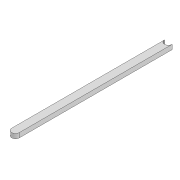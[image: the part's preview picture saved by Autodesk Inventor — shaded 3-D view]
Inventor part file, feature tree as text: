
AUTODESK INVENTOR PART (.ipt)
format: ipt  version: 2022 (Build 260153000, 153)  size: 77,824 bytes
history: native  units: mm
features: extrude x1, sketch x1
ambient origin geometry x8: Origin, YZ Plane, XZ Plane, XY Plane, X Axis, Y Axis, Z Axis, Center Point
bodies: Solid1 (feature_tree)
feature tree (2):
  extrude  "Extrusion1"  Depth=10.0mm
  sketch  "Sketch1"  dims[d0=200.0mm d1=10.0mm d2=6.0mm d3=0.0mm]
